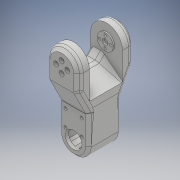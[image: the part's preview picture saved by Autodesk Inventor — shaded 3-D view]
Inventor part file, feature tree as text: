
AUTODESK INVENTOR PART (.ipt)
format: ipt  version: 2018 (Build 220112000, 112)  size: 1,053,696 bytes
history: native  units: mm
features: projected_geometry x42, sketch x40, extrude x33, fillet x13, chamfer x11, hole x8, other x4, mirror x1, reference x1
ambient origin geometry x8: Origin, YZ Plane, XZ Plane, XY Plane, X Axis, Y Axis, Z Axis, Center Point
bodies: Solid1 (feature_tree)
feature tree (153):
  extrude  "Extrusion1"  Depth=45.0mm
  extrude  "Extrusion2"  Depth=2.25mm
  hole  "Hole1"  [1 undecoded]
  hole  "Hole2"  [1 undecoded]
  fillet  "Fillet1"  Radius=14.0mm
  extrude  "Extrusion3"  Depth=18.5mm
  extrude  "Extrusion4"  Depth=10.0mm
  extrude  "Extrusion5"  Depth=2.0mm
  extrude  "Extrusion6"  Depth=2.0mm
  hole  "Hole3"  [1 undecoded]
  extrude  "Extrusion7"  Depth=0.5mm
  extrude  "Extrusion8"  Depth=5.0mm TaperAngle=0.0deg
  extrude  "Extrusion9"  Depth=10.0mm
  extrude  "Extrusion10"  Depth=10.0mm
  extrude  "Extrusion11"  Depth=14.5mm
  extrude  "Extrusion12"  Depth=20.0mm
  extrude  "Extrusion13"  Depth=5.0mm
  extrude  "Extrusion14"  Depth=5.0mm
  extrude  "Extrusion15"  Depth=5.0mm
  extrude  "Extrusion16"  Depth=5.0mm
  extrude  "Extrusion17"  Depth=1.0mm
  chamfer  "Chamfer1"  Distance=1.0mm
  fillet  "Fillet7"  Radius=20.7mm
  fillet  "Fillet8"  Radius=32.0mm
  mirror  "Mirror1"
  extrude  "Extrusion19"  Depth=1.0mm TaperAngle=0.0deg
  extrude  "Extrusion20"  Depth=8.0mm
  extrude  "Extrusion21"  Depth=0.2mm TaperAngle=0.0deg
  extrude  "Extrusion22"  Depth=0.5mm TaperAngle=0.0deg
  extrude  "Extrusion23"  Depth=9.0mm TaperAngle=0.0deg
  extrude  "Extrusion24"  Depth=2.0mm TaperAngle=0.0deg
  chamfer  "Chamfer2"  Distance=0.2mm
  chamfer  "Chamfer8"  Distance=2.0mm Angle=45.0deg
  extrude  "Extrusion25"  Depth=0.5mm
  extrude  "Extrusion26"  Depth=2.0mm TaperAngle=0.0deg
  chamfer  "Chamfer3"  Distance=2.0mm
  chamfer  "Chamfer4"  Distance=2.0mm
  chamfer  "Chamfer5"  Distance=15.0mm
  chamfer  "Chamfer6"  Distance=56.1mm
  fillet  "Fillet9"  Radius=41.6mm
  fillet  "Fillet10"  Radius=41.0mm
  hole  "Hole6"  [1 undecoded]
  fillet  "Fillet12"  Radius=7.0mm
  hole  "Hole7"  [1 undecoded]
  extrude  "Extrusion27"  Depth=3.0mm TaperAngle=45.0deg
  extrude  "Extrusion28"  Depth=5.0mm TaperAngle=45.0deg
  hole  "Hole8"  [1 undecoded]
  extrude  "Extrusion29"  Depth=2.0mm
  chamfer  "Chamfer7"  Distance=1.0mm
  fillet  "Fillet13"  Radius=20.5mm
  extrude  "Extrusion30"  Depth=1.0mm TaperAngle=0.0deg
  extrude  "Extrusion31"  Depth=1.0mm
  fillet  "Fillet14"  Radius=3.1mm
  extrude  "Extrusion32"  Depth=14.0mm
  fillet  "Fillet15"  Radius=16.0mm
  fillet  "Fillet18"  Radius=3.1mm
  extrude  "Extrusion35"  Depth=2.0mm TaperAngle=45.0deg
  extrude  "Extrusion36"  Depth=1.0mm
  chamfer  "Chamfer9"  Distance=37.0mm
  chamfer  "Chamfer10"  Distance=10.0mm
  chamfer  "Chamfer11"  Distance=7.5mm
  fillet  "Fillet19"  Radius=6.0mm
  hole  "Hole9"  [1 undecoded]
  fillet  "Fillet20"  Radius=6.0mm
  hole  "Hole10"  [1 undecoded]
  fillet  "Fillet21"  Radius=5.0mm
  sketch  "Sketch1"  dims[d0=24.5mm d1=45.0mm]
  sketch  "Sketch2"  dims[d2=1.95mm d3=0.0mm d4=2.25mm]
  projected_geometry  "Projected Loop1"
  sketch  "Sketch3"  dims[d5=20.0mm d6=2.25mm]
  projected_geometry  "Projected Loop2"
  sketch  "Sketch4"  dims[d7=5.25mm d8=5.25mm d9=14.0mm]
  projected_geometry  "Projected Loop3"
  sketch  "Sketch5"  dims[d10=5.25mm d11=18.5mm]
  projected_geometry  "Projected Loop4"
  sketch  "Sketch6"  dims[d12=10.0mm d13=0.0mm d14=20.5mm]
  projected_geometry  "Projected Loop5"
  sketch  "Sketch7"  dims[d15=2.0mm d16=2.195mm]
  projected_geometry  "Projected Loop6"
  sketch  "Sketch8"  dims[d17=2.0mm]
  projected_geometry  "Projected Loop7"
  sketch  "Sketch9"  dims[d18=2.4mm d19=6.0mm d20=4.4mm d21=2.0mm d22=90.0deg d23=8.0mm d24=20.594885mm d25=20.5mm]
  projected_geometry  "Projected Loop8"
  projected_geometry  "Projected Loop9"
  sketch  "Sketch10"  dims[d26=26.65mm d27=2.0mm]
  projected_geometry  "Projected Loop10"
  projected_geometry  "Projected Loop11"
  sketch  "Sketch11"  dims[d28=2.0mm]
  projected_geometry  "Projected Loop12"
  sketch  "Sketch12"  dims[d29=2.4mm d30=6.0mm d31=4.4mm d32=2.0mm d33=90.0deg d34=8.0mm d35=20.594885mm d36=0.5mm]
  sketch  "Sketch13"  dims[d37=18.0mm d38=5.0mm d39=0.0mm]
  sketch  "Sketch14"  dims[d41=10.0mm d42=0.0mm d43=24.5mm]
  projected_geometry  "Projected Loop13"
  sketch  "Sketch15"  dims[d44=1.15mm d45=0.0mm d46=10.0mm]
  sketch  "Sketch16"  dims[d47=21.0mm d48=14.5mm]
  projected_geometry  "Projected Loop14"
  sketch  "Sketch17"  dims[d49=20.0mm d50=14.5mm]
  projected_geometry  "Projected Loop15"
  sketch  "Sketch18"  dims[d51=24.5mm d52=5.0mm]
  projected_geometry  "Projected Loop16"
  sketch  "Sketch19"  dims[d53=5.0mm d54=2.25mm]
  projected_geometry  "Projected Loop17"
  sketch  "Sketch20"  dims[d55=2.25mm d56=5.0mm]
  projected_geometry  "Projected Loop18"
  sketch  "Sketch25"  dims[d57=5.0mm d58=9.0mm]
  projected_geometry  "Projected Loop22"
  sketch  "Sketch26"  dims[d59=14.75mm d60=4.0mm d61=1.0mm d62=0.0mm d63=20.7mm]
  projected_geometry  "Projected Loop23"
  sketch  "Sketch27"  dims[d64=2.4mm d65=6.0mm d66=4.4mm d67=2.0mm d68=90.0deg d69=8.0mm d70=20.594885mm d72=32.0mm]
  projected_geometry  "Projected Loop24"
  sketch  "Sketch28"  dims[d73=5.0mm d74=0.0mm d75=1.0mm d76=0.0mm]
  projected_geometry  "Projected Loop25"
  sketch  "Sketch29"  dims[d77=12.25mm d78=0.0mm d80=8.0mm]
  projected_geometry  "Projected Loop26"
  sketch  "Sketch30"  dims[d81=4.5mm d82=0.0mm d84=0.2mm d85=0.0mm]
  projected_geometry  "Projected Loop27"
  sketch  "Sketch31"  dims[d86=21.0mm d87=0.5mm d88=0.0mm]
  sketch  "Sketch33"  dims[d91=8.0mm d92=0.0mm d93=9.0mm d94=0.0mm]
  projected_geometry  "Projected Loop28"
  projected_geometry  "Projected Loop29"
  projected_geometry  "Projected Loop30"
  sketch  "Sketch34"  dims[d95=5.0mm d96=0.0mm d98=0.2mm d99=0.0mm d100=0.2mm d101=0.0mm d102=2.5mm d103=2.0mm d104=45.0deg]
  projected_geometry  "Projected Loop31"
  projected_geometry  "Projected Loop32"
  sketch  "Sketch35"  dims[d105=1.5mm d114=0.5mm]
  projected_geometry  "Projected Loop33"
  sketch  "Sketch36"  dims[d128=2.0mm d129=0.0mm d130=2.0mm d131=0.0mm]
  projected_geometry  "Projected Loop34"
  sketch  "Sketch37"  dims[d132=40.0mm d133=2.0mm d134=0.0mm d135=2.0mm d136=0.0mm]
  projected_geometry  "Projected Loop35"
  sketch  "Sketch38"  dims[d137=40.0mm]
  projected_geometry  "Projected Loop36"
  sketch  "Sketch39"  dims[d138=70.0mm d139=15.0mm d140=0.0mm d141=56.1mm d142=0.0mm]
  projected_geometry  "Projected Loop37"
  sketch  "Sketch40"  dims[d143=4.0mm d144=8.0mm d145=45.0deg d146=41.6mm d147=41.0mm]
  projected_geometry  "Projected Loop38"
  sketch  "Sketch41"  dims[d148=7.0mm d149=7.0mm d150=7.0mm]
  projected_geometry  "Projected Loop39"
  reference  "Reference1"
  sketch  "Sketch44"  dims[d151=100.0mm d152=0.0mm d153=15.282752mm]
  projected_geometry  "Projected Loop42"
  sketch  "Sketch45"  dims[d156=100.0mm d157=0.0mm d158=3.0mm d159=2.0mm d160=45.0deg]
  projected_geometry  "Projected Loop43"
  sketch  "Sketch46"  dims[d161=5.0mm d162=2.0mm d163=45.0deg d164=5.0mm d165=2.0mm d166=45.0deg]
  projected_geometry  "Projected Loop44"
  sketch  "Sketch47"  dims[d167=5.0mm d168=2.0mm d169=45.0deg d170=5.0mm d171=2.0mm d173=5.7mm d174=6.0mm d175=4.0mm d176=2.0mm d177=90.0deg d178=25.0mm d179=0.0mm d180=1.0mm d181=2.459mm d182=25.0mm d183=4.0mm d184=2.0mm d185=90.0deg d186=25.0mm d187=20.594885mm d188=20.5mm d189=1.6mm d190=0.0mm d191=20.5mm d192=3.1mm d193=0.0mm d194=14.0mm d195=3.2mm d196=25.0mm d197=6.3mm d198=2.0mm d199=90.0deg d200=25.0mm d201=20.594885mm d202=16.0mm d203=3.1mm d204=0.0mm d205=1.5mm d206=2.0mm d207=45.0deg d208=1.7mm d209=37.0mm d210=10.0mm d211=0.0mm d212=7.5mm d213=6.0mm d214=6.0mm d215=6.0mm d216=6.0mm d217=5.0mm d218=0.0mm d219=1.5mm d220=6.0mm d221=6.0mm d222=6.0mm d223=6.0mm d224=6.0mm d225=0.0mm d226=1.5mm d231=4.0mm d232=8.0mm d233=45.0deg d234=10.0mm d237=7.0mm d238=2.5mm d239=0.0mm d240=7.0mm d241=2.5mm d242=0.0mm d243=14.0mm d244=25.0mm d245=45.0deg d246=14.0mm d247=25.0mm d248=45.0deg d249=14.0mm d250=25.0mm d251=45.0deg d252=10.0mm d253=4.0mm d254=6.0mm d255=4.0mm d256=2.0mm d257=90.0deg d258=2.0mm d259=20.594885mm d260=1.0mm d261=4.0mm d262=6.0mm d263=4.0mm d264=2.0mm d265=90.0deg d266=2.0mm d267=20.594885mm d268=1.0mm]
  projected_geometry  "Projected Loop45"
  projected_geometry  "Project Cut Edges1"
  projected_geometry  "Project Cut Edges2"
  parser-record x1  (decoder bookkeeping rows leaked as tree rows — omitted from the tree; the rows remain in map.json)
  other  "servocheck.iam"
  other  "bottomarm:1"
  other  "arm1:1"
note: 8 required parameter values undecoded (feature->parameter linkage not recoverable at this tier; creation-order binding heuristic only, values carry confidence <= 0.55)
note: 1 file-system path scrubbed to <path> (originals preserved in map.json)
